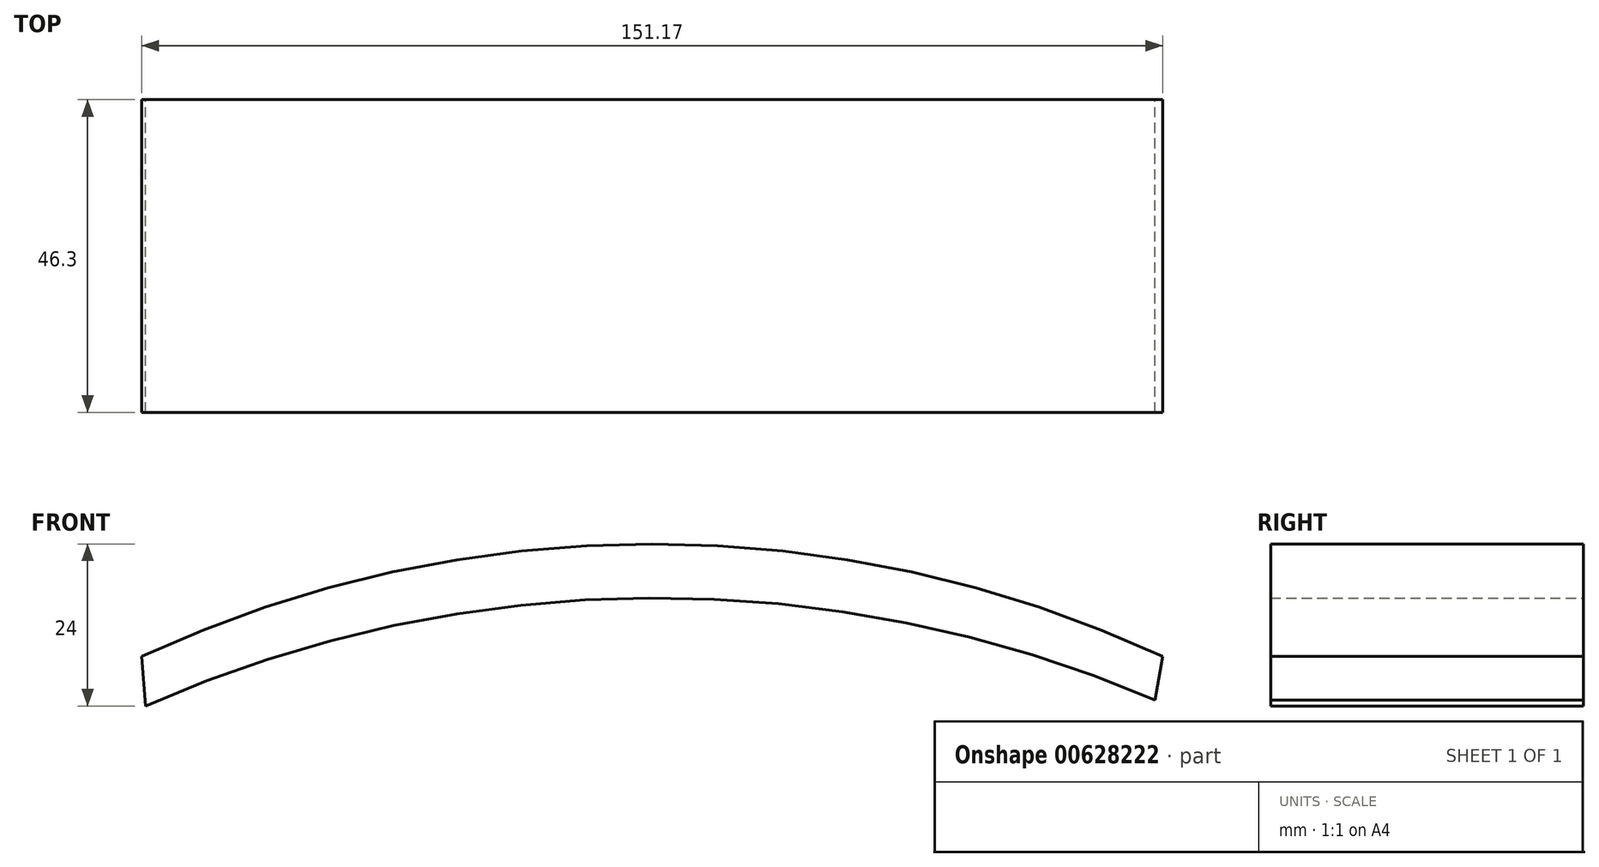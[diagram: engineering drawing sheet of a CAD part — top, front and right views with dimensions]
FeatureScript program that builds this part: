
annotation { "Feature Type Name" : "Feature", "Feature Type Description" : "" }
export const myFeature = defineFeature(function(context is Context, id is Id, definition is map)
    precondition{}
    {
        {
            var Q0;
            Q0=qCreatedBy(makeId("Front.planeOp"),FACE);
            var sketch = newSketch(context, id + "F0", { "sketchPlane" : qUnion([Q0])});
            skArc(sketch, "E0", {"start": v(75.73, 0) * mm, "mid": v(0.14, 16.67) * mm, "end": v(-75.44, 0) * mm});
            skArc(sketch, "E1", {"start": v(74.58, -6.47) * mm, "mid": v(-0.23, 8.66) * mm, "end": v(-74.87, -7.33) * mm});
            skLineSegment(sketch, "E2", {"start": v(-75.44, 0) * mm, "end": v(-74.87, -7.33) * mm});
            skLineSegment(sketch, "E3", {"start": v(75.73, 0) * mm, "end": v(74.58, -6.47) * mm});
            skSolve(sketch);
        }
        {
            var Q0;
            Q0=makeQuery(id+"F0.imprint","IMPRINT",FACE,{"disambiguationData":[TD([[makeQuery(id+"F0.imprint","IMPRINT",EDGE,{"derivedFrom":sQuery(id+"F0.wireOp",EDGE,"E0")}),1.0]])]});
            extrude(context, id + "F1", {"entities" : qUnion([Q0]), "depth" : 46.3 * mm, "offsetDistance" : 25 * mm});
        }
    });
